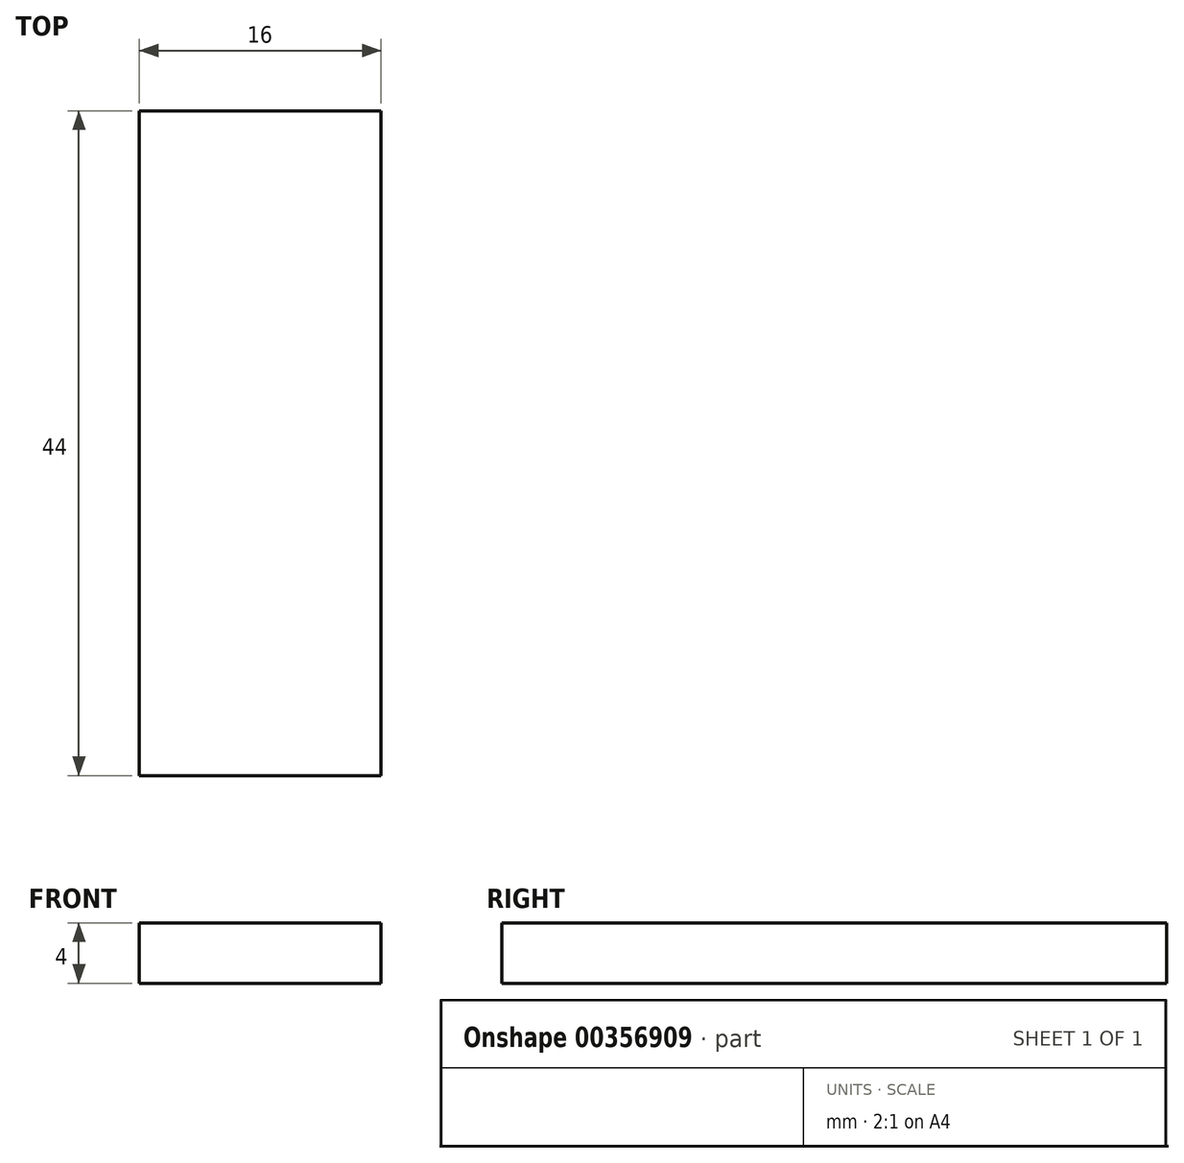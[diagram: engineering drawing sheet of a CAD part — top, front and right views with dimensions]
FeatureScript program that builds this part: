
annotation { "Feature Type Name" : "Feature", "Feature Type Description" : "" }
export const myFeature = defineFeature(function(context is Context, id is Id, definition is map)
    precondition{}
    {
        {
            var Q0;
            Q0=qCreatedBy(makeId("Top.planeOp"),FACE);
            var sketch = newSketch(context, id + "F0", { "sketchPlane" : qUnion([Q0])});
            skLineSegment(sketch, "E0.bottom", {"start": v(-8, 22) * mm, "end": v(8, 22) * mm});
            skLineSegment(sketch, "E0.top", {"start": v(-8, -22) * mm, "end": v(8, -22) * mm});
            skLineSegment(sketch, "E0.left", {"start": v(-8, 22) * mm, "end": v(-8, -22) * mm});
            skLineSegment(sketch, "E0.right", {"start": v(8, 22) * mm, "end": v(8, -22) * mm});
            skPoint(sketch, "E0.middle", {"position": v(0, 0) * mm});
            skSolve(sketch);
        }
        {
            var Q0;
            Q0=qSketchRegion(id+"F0",true);
            extrude(context, id + "F1", {"entities" : qUnion([Q0]), "depth" : 4 * mm});
        }
    });
